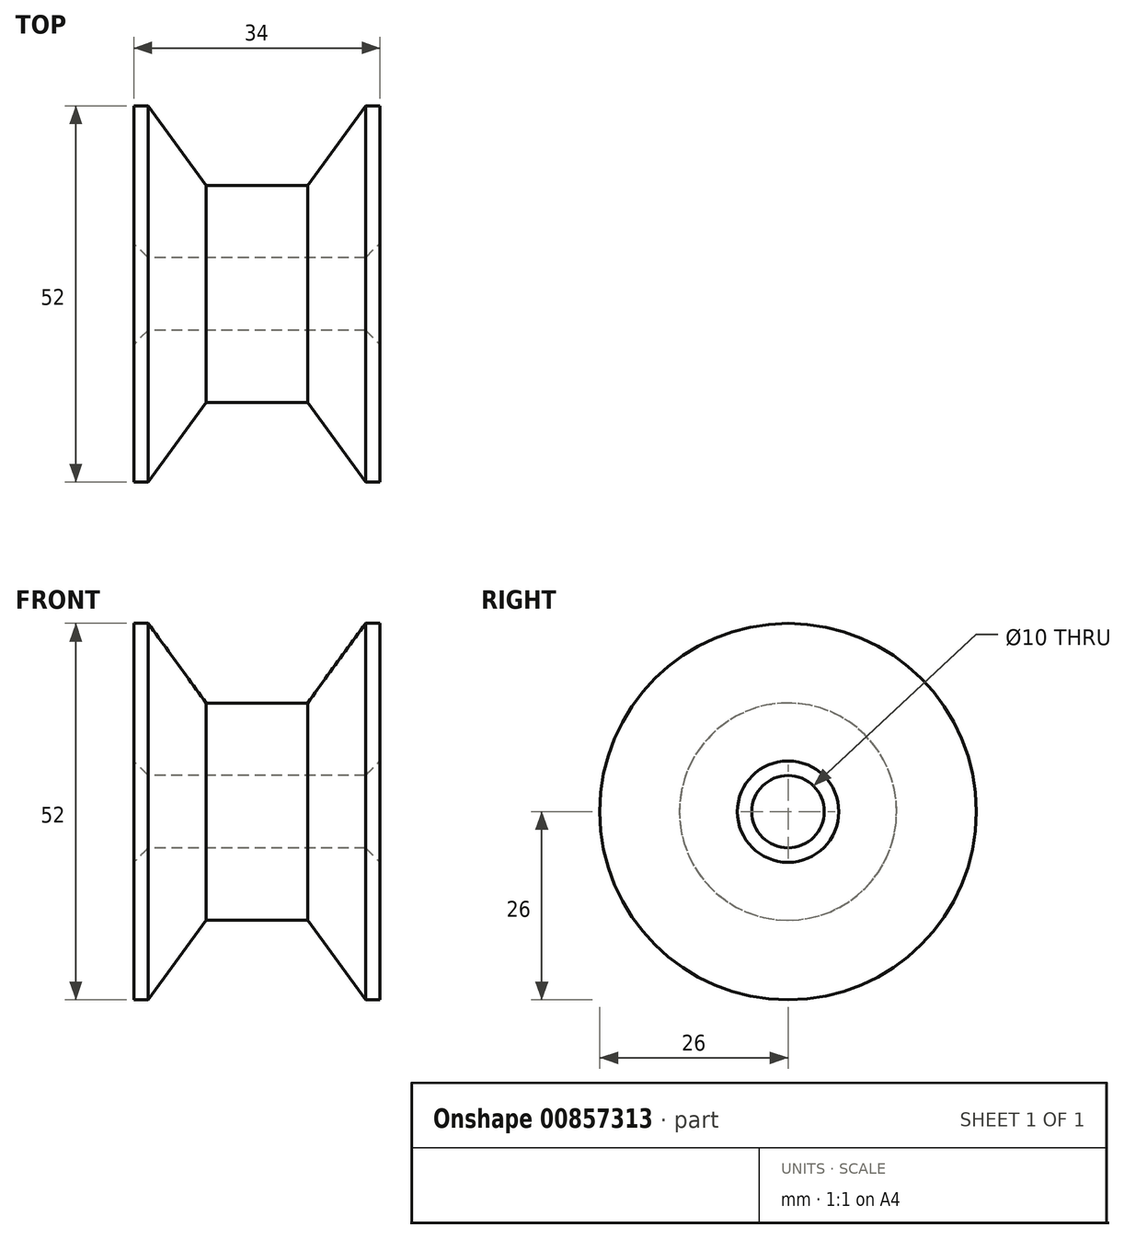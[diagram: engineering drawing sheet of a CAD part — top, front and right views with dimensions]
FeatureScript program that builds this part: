
annotation { "Feature Type Name" : "Feature", "Feature Type Description" : "" }
export const myFeature = defineFeature(function(context is Context, id is Id, definition is map)
    precondition{}
    {
        {
            var Q0;
            Q0=qCreatedBy(makeId("Front.planeOp"),FACE);
            var sketch = newSketch(context, id + "F0", { "sketchPlane" : qUnion([Q0])});
            skLineSegment(sketch, "E0", {"start": v(0, 0) * mm, "end": v(34, 0) * mm});
            skLineSegment(sketch, "E1", {"start": v(0, 5) * mm, "end": v(34, 5) * mm});
            skLineSegment(sketch, "E2", {"start": v(34, 5) * mm, "end": v(34, 26) * mm});
            skLineSegment(sketch, "E3", {"start": v(34, 26) * mm, "end": v(32, 26) * mm});
            skLineSegment(sketch, "E4", {"start": v(32, 26) * mm, "end": v(32, 15) * mm});
            skLineSegment(sketch, "E5", {"start": v(32, 15) * mm, "end": v(2, 15) * mm});
            skLineSegment(sketch, "E6", {"start": v(2, 15) * mm, "end": v(2, 26) * mm});
            skLineSegment(sketch, "E7", {"start": v(2, 26) * mm, "end": v(0, 26) * mm});
            skLineSegment(sketch, "E8", {"start": v(0, 26) * mm, "end": v(0, 5) * mm});
            skSolve(sketch);
        }
        {
            var Q0;
            Q0=makeQuery(id+"F0.imprint","IMPRINT",FACE,{"disambiguationData":[TD([[makeQuery(id+"F0.imprint","IMPRINT",EDGE,{"derivedFrom":sQuery(id+"F0.wireOp",EDGE,"E1")}),1.0]])]});
            var Q1;
            Q1=sQuery(id+"F0.wireOp",EDGE,"E0");
            revolve(context, id + "F1", {"surfaceOperationType" : NewSurfaceOperationType.NEW, "entities" : qUnion([Q0]), "axis" : qUnion([Q1]), "revolveType" : RevolveType.FULL});
        }
        {
            var Q0;
            Q0=makeQuery(id+"F1.opRevolve","SWEPT_EDGE",EDGE,{"disambiguationData":[OSD([sQuery(id+"F0.wireOp",EDGE,"E5"),sQuery(id+"F0.wireOp",EDGE,"E6")])]});
            var Q1;
            Q1=makeQuery(id+"F1.opRevolve","SWEPT_EDGE",EDGE,{"disambiguationData":[OSD([sQuery(id+"F0.wireOp",EDGE,"E4"),sQuery(id+"F0.wireOp",EDGE,"E5")])]});
            chamfer(context, id + "F2", {"entities" : qUnion([Q0, Q1]), "chamferType" : ChamferType.TWO_OFFSETS, "width1" : 11 * mm, "oppositeDirection" : false, "width2" : 8 * mm, "tangentPropagation" : true});
        }
        {
            var Q0;
            Q0=makeQuery(id+"F1.opRevolve","SWEPT_EDGE",EDGE,{"disambiguationData":[OSD([sQuery(id+"F0.wireOp",EDGE,"E1"),sQuery(id+"F0.wireOp",EDGE,"E8")])]});
            var Q1;
            Q1=makeQuery(id+"F1.opRevolve","SWEPT_EDGE",EDGE,{"disambiguationData":[OSD([sQuery(id+"F0.wireOp",EDGE,"E1"),sQuery(id+"F0.wireOp",EDGE,"E2")])]});
            chamfer(context, id + "F3", {"entities" : qUnion([Q0, Q1]), "width" : 2 * mm, "tangentPropagation" : true});
        }
    });
